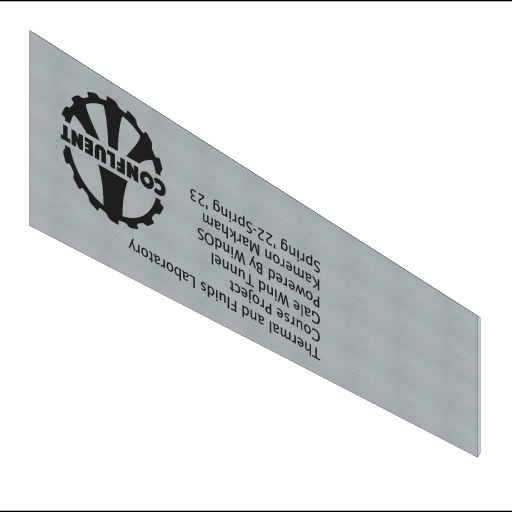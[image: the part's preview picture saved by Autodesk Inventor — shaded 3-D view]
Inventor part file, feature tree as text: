
AUTODESK INVENTOR PART (.ipt)
format: ipt  version: 2023 (Build 270158000, 158)  size: 3,141,632 bytes
history: native  units: in
note: dims shown in document units (in); Inventor stores cm internally (conversion verified against a paired STEP export)
features: sketch x9, extrude x5, loft x2, projected_geometry x2, other x1
ambient origin geometry x8: Origin, YZ Plane, XZ Plane, XY Plane, X Axis, Y Axis, Z Axis, Center Point
bodies: Solid1 (feature_tree)
feature tree (19):
  extrude  "Extrusion1"  Depth=18.1in
  loft  "Loft1"
  loft  "Loft2"
  other  "Center Plane"
  extrude  "Extrusion2"  Depth=0.9279in
  extrude  "Extrusion3"  TaperAngle=0.0deg  [1 undecoded]
  extrude  "Extrusion4"  Depth=0.3089in
  extrude  "Extrusion5"  TaperAngle=0.0deg  [1 undecoded]
  sketch  "Sketch1"  dims[d0=48.0in d1=18.1in]
  sketch  "Sketch2"  dims[d2=1.0in d3=13.1in]
  sketch  "Sketch3"  dims[d4=2.5in d5=0.5in d6=0.0in]
  sketch  "Sketch4"  dims[d7=0.3089in d8=0.9279in]
  sketch  "Sketch5"  dims[d9=0.0in d10=90.0deg d11=0.0in d12=90.0deg]
  sketch  "Sketch6"  dims[d13=0.9279in d14=0.3089in]
  sketch  "Sketch8"  dims[d15=0.0in d16=90.0deg d17=0.0in d18=90.0deg]
  projected_geometry  "Projected Loop2"
  sketch  "Sketch9"  dims[d19=9.0in]
  projected_geometry  "Projected Loop3"
  sketch  "Sketch10"  dims[d21=6.5in d22=0.0in d26=0.5979in d27=0.227in d28=1.0in d29=1.0in d30=1.0in d31=0.0in d32=0.6389in d33=9.0286in d34=0.0in d63=0.005in d64=0.0in]
note: 2 required parameter values undecoded (feature->parameter linkage not recoverable at this tier; creation-order binding heuristic only, values carry confidence <= 0.55)
